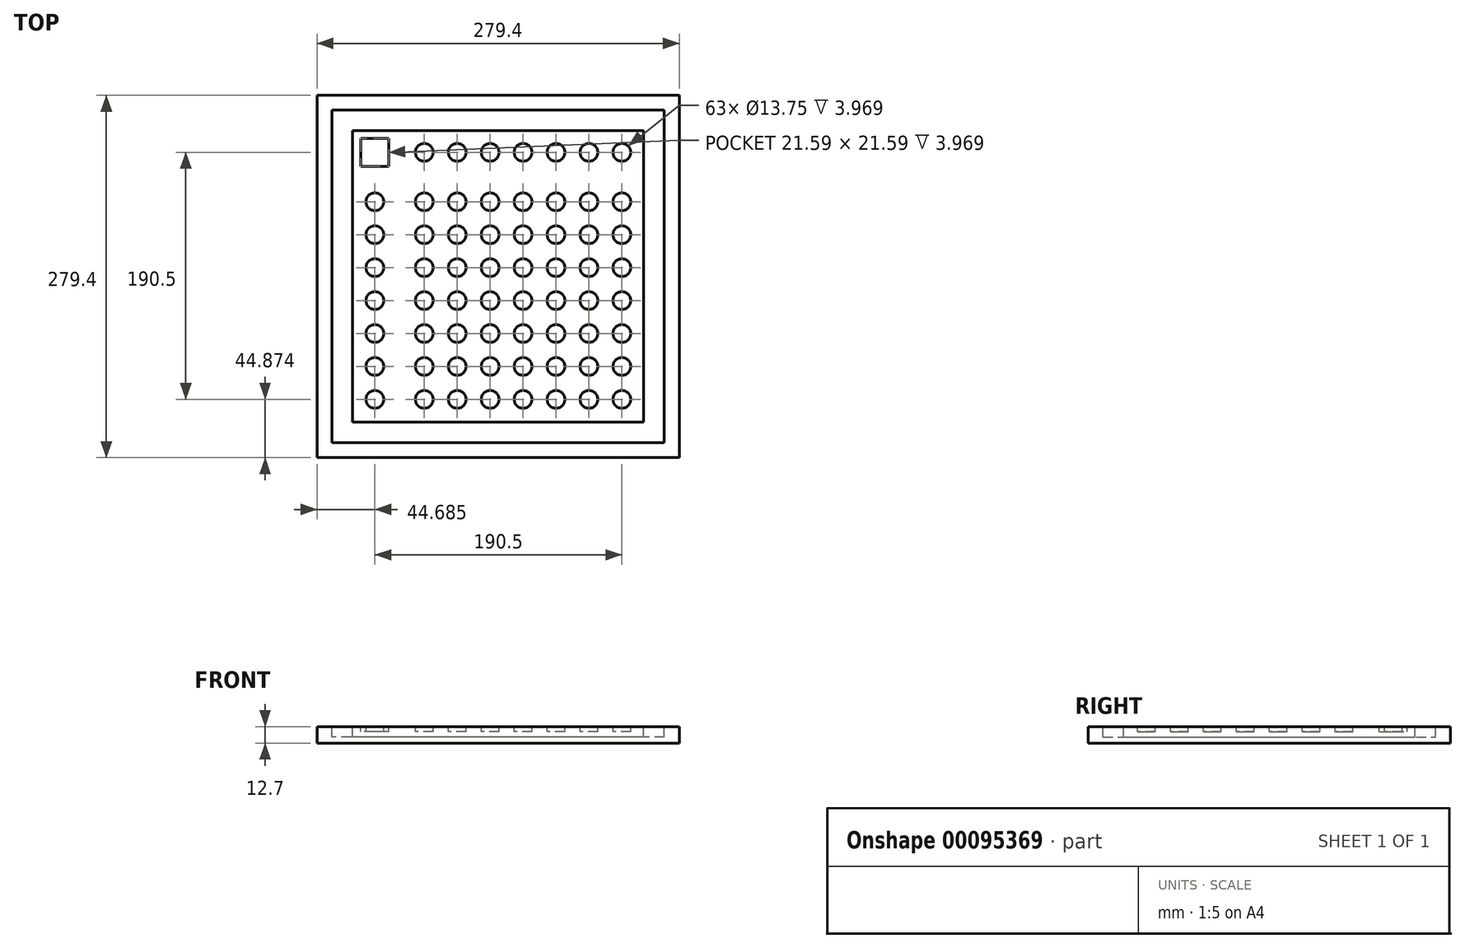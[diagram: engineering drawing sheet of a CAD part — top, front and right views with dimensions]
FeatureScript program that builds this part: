
annotation { "Feature Type Name" : "Feature", "Feature Type Description" : "" }
export const myFeature = defineFeature(function(context is Context, id is Id, definition is map)
    precondition{}
    {
        {
            var Q0;
            Q0=qCreatedBy(makeId("Top.planeOp"),FACE);
            var sketch = newSketch(context, id + "F0", { "sketchPlane" : qUnion([Q0])});
            skLineSegment(sketch, "E0.bottom", {"start": v(-139.7, -139.7) * mm, "end": v(139.7, -139.7) * mm});
            skLineSegment(sketch, "E0.top", {"start": v(-139.7, 139.7) * mm, "end": v(139.7, 139.7) * mm});
            skLineSegment(sketch, "E0.left", {"start": v(-139.7, -139.7) * mm, "end": v(-139.7, 139.7) * mm});
            skLineSegment(sketch, "E0.right", {"start": v(139.7, -139.7) * mm, "end": v(139.7, 139.7) * mm});
            skPoint(sketch, "E0.middle", {"position": v(0, 0) * mm});
            skSolve(sketch);
        }
        {
            var Q0;
            Q0 = qSketchRegion(id + "F0", true);
            extrude(context, id + "F1", {"entities" : qUnion([Q0]), "oppositeDirection" : true, "depth" : 12.7 * mm});
        }
        {
            var Q0;
            Q0=qCreatedBy(makeId("Top.planeOp"),FACE);
            var sketch = newSketch(context, id + "F2", { "sketchPlane" : qUnion([Q0])});
            skCircle(sketch, "E1", {"center": v(-56.91, -94.83) * mm, "radius": 6.87 * mm});
            skPoint(sketch, "E1.first.point", {"position": v(-63.74, -95.66) * mm});
            skPoint(sketch, "E1.second.point", {"position": v(-63.74, -95.66) * mm});
            skPoint(sketch, "E1.third.point", {"position": v(-63.74, -95.66) * mm});
            skCircle(sketch, "E2.0.1.0", {"center": v(-56.91, -69.43) * mm, "radius": 6.87 * mm});
            skCircle(sketch, "E2.0.2.0", {"center": v(-56.91, -44.03) * mm, "radius": 6.87 * mm});
            skCircle(sketch, "E2.0.3.0", {"center": v(-56.91, -18.63) * mm, "radius": 6.87 * mm});
            skCircle(sketch, "E2.0.4.0", {"center": v(-56.91, 6.77) * mm, "radius": 6.87 * mm});
            skCircle(sketch, "E2.0.5.0", {"center": v(-56.91, 32.17) * mm, "radius": 6.87 * mm});
            skCircle(sketch, "E2.0.6.0", {"center": v(-56.91, 57.57) * mm, "radius": 6.87 * mm});
            skCircle(sketch, "E2.1.0.0", {"center": v(-31.51, -94.83) * mm, "radius": 6.87 * mm});
            skCircle(sketch, "E2.1.1.0", {"center": v(-31.51, -69.43) * mm, "radius": 6.87 * mm});
            skCircle(sketch, "E2.1.2.0", {"center": v(-31.51, -44.03) * mm, "radius": 6.87 * mm});
            skCircle(sketch, "E2.1.3.0", {"center": v(-31.51, -18.63) * mm, "radius": 6.87 * mm});
            skCircle(sketch, "E2.1.4.0", {"center": v(-31.51, 6.77) * mm, "radius": 6.87 * mm});
            skCircle(sketch, "E2.1.5.0", {"center": v(-31.51, 32.17) * mm, "radius": 6.87 * mm});
            skCircle(sketch, "E2.1.6.0", {"center": v(-31.51, 57.57) * mm, "radius": 6.87 * mm});
            skCircle(sketch, "E2.2.0.0", {"center": v(-6.11, -94.83) * mm, "radius": 6.87 * mm});
            skCircle(sketch, "E2.2.1.0", {"center": v(-6.11, -69.43) * mm, "radius": 6.87 * mm});
            skCircle(sketch, "E2.2.2.0", {"center": v(-6.11, -44.03) * mm, "radius": 6.87 * mm});
            skCircle(sketch, "E2.2.3.0", {"center": v(-6.11, -18.63) * mm, "radius": 6.87 * mm});
            skCircle(sketch, "E2.2.4.0", {"center": v(-6.11, 6.77) * mm, "radius": 6.87 * mm});
            skCircle(sketch, "E2.2.5.0", {"center": v(-6.11, 32.17) * mm, "radius": 6.87 * mm});
            skCircle(sketch, "E2.2.6.0", {"center": v(-6.11, 57.57) * mm, "radius": 6.87 * mm});
            skCircle(sketch, "E2.3.0.0", {"center": v(19.29, -94.83) * mm, "radius": 6.87 * mm});
            skCircle(sketch, "E2.3.1.0", {"center": v(19.29, -69.43) * mm, "radius": 6.87 * mm});
            skCircle(sketch, "E2.3.2.0", {"center": v(19.29, -44.03) * mm, "radius": 6.87 * mm});
            skCircle(sketch, "E2.3.3.0", {"center": v(19.29, -18.63) * mm, "radius": 6.87 * mm});
            skCircle(sketch, "E2.3.4.0", {"center": v(19.29, 6.77) * mm, "radius": 6.87 * mm});
            skCircle(sketch, "E2.3.5.0", {"center": v(19.29, 32.17) * mm, "radius": 6.87 * mm});
            skCircle(sketch, "E2.3.6.0", {"center": v(19.29, 57.57) * mm, "radius": 6.87 * mm});
            skCircle(sketch, "E2.4.0.0", {"center": v(44.69, -94.83) * mm, "radius": 6.87 * mm});
            skCircle(sketch, "E2.4.1.0", {"center": v(44.69, -69.43) * mm, "radius": 6.87 * mm});
            skCircle(sketch, "E2.4.2.0", {"center": v(44.69, -44.03) * mm, "radius": 6.87 * mm});
            skCircle(sketch, "E2.4.3.0", {"center": v(44.69, -18.63) * mm, "radius": 6.87 * mm});
            skCircle(sketch, "E2.4.4.0", {"center": v(44.69, 6.77) * mm, "radius": 6.87 * mm});
            skCircle(sketch, "E2.4.5.0", {"center": v(44.69, 32.17) * mm, "radius": 6.87 * mm});
            skCircle(sketch, "E2.4.6.0", {"center": v(44.69, 57.57) * mm, "radius": 6.87 * mm});
            skCircle(sketch, "E2.5.0.0", {"center": v(70.09, -94.83) * mm, "radius": 6.87 * mm});
            skCircle(sketch, "E2.5.1.0", {"center": v(70.09, -69.43) * mm, "radius": 6.87 * mm});
            skCircle(sketch, "E2.5.2.0", {"center": v(70.09, -44.03) * mm, "radius": 6.87 * mm});
            skCircle(sketch, "E2.5.3.0", {"center": v(70.09, -18.63) * mm, "radius": 6.87 * mm});
            skCircle(sketch, "E2.5.4.0", {"center": v(70.09, 6.77) * mm, "radius": 6.87 * mm});
            skCircle(sketch, "E2.5.5.0", {"center": v(70.09, 32.17) * mm, "radius": 6.87 * mm});
            skCircle(sketch, "E2.5.6.0", {"center": v(70.09, 57.57) * mm, "radius": 6.87 * mm});
            skCircle(sketch, "E2.6.0.0", {"center": v(95.49, -94.83) * mm, "radius": 6.87 * mm});
            skCircle(sketch, "E2.6.1.0", {"center": v(95.49, -69.43) * mm, "radius": 6.87 * mm});
            skCircle(sketch, "E2.6.2.0", {"center": v(95.49, -44.03) * mm, "radius": 6.87 * mm});
            skCircle(sketch, "E2.6.3.0", {"center": v(95.49, -18.63) * mm, "radius": 6.87 * mm});
            skCircle(sketch, "E2.6.4.0", {"center": v(95.49, 6.77) * mm, "radius": 6.87 * mm});
            skCircle(sketch, "E2.6.5.0", {"center": v(95.49, 32.17) * mm, "radius": 6.87 * mm});
            skCircle(sketch, "E2.6.6.0", {"center": v(95.49, 57.57) * mm, "radius": 6.87 * mm});
            skLineSegment(sketch, "E2.direction1", {"start": v(-56.91, -94.83) * mm, "end": v(-31.51, -94.83) * mm, "construction": true});
            skLineSegment(sketch, "E2.direction2", {"start": v(-56.91, -94.83) * mm, "end": v(-56.91, -69.43) * mm, "construction": true});
            skCircle(sketch, "E3", {"center": v(-95.01, -94.83) * mm, "radius": 6.87 * mm});
            skPoint(sketch, "E3.first.point", {"position": v(-101.85, -94.1) * mm});
            skPoint(sketch, "E3.second.point", {"position": v(-101.85, -94.1) * mm});
            skPoint(sketch, "E3.third.point", {"position": v(-101.85, -94.1) * mm});
            skLineSegment(sketch, "E4.direction2", {"start": v(-95.01, -94.83) * mm, "end": v(-95.01, -74.61) * mm, "construction": true});
            skCircle(sketch, "E5", {"center": v(95.49, 95.67) * mm, "radius": 6.87 * mm});
            skPoint(sketch, "E5.first.point", {"position": v(100.9, 99.9) * mm});
            skPoint(sketch, "E5.second.point", {"position": v(100.9, 99.9) * mm});
            skPoint(sketch, "E5.third.point", {"position": v(100.9, 99.9) * mm});
            skCircle(sketch, "E6.1.0.0", {"center": v(70.09, 95.67) * mm, "radius": 6.87 * mm});
            skCircle(sketch, "E6.2.0.0", {"center": v(44.69, 95.67) * mm, "radius": 6.87 * mm});
            skCircle(sketch, "E6.3.0.0", {"center": v(19.29, 95.67) * mm, "radius": 6.87 * mm});
            skCircle(sketch, "E6.4.0.0", {"center": v(-6.11, 95.67) * mm, "radius": 6.87 * mm});
            skCircle(sketch, "E6.5.0.0", {"center": v(-31.51, 95.67) * mm, "radius": 6.87 * mm});
            skCircle(sketch, "E6.6.0.0", {"center": v(-56.91, 95.67) * mm, "radius": 6.87 * mm});
            skLineSegment(sketch, "E6.direction1", {"start": v(95.49, 95.67) * mm, "end": v(70.09, 95.67) * mm, "construction": true});
            skPoint(sketch, "E7.first.point", {"position": v(-88.23, 95.76) * mm});
            skPoint(sketch, "E7.second.point", {"position": v(-88.23, 95.76) * mm});
            skPoint(sketch, "E7.third.point", {"position": v(-88.23, 95.76) * mm});
            skPoint(sketch, "E8.middle", {"position": v(11.35, 8.36) * mm});
            skCircle(sketch, "E9.0.1.0", {"center": v(-95.01, -69.43) * mm, "radius": 6.87 * mm});
            skCircle(sketch, "E9.0.2.0", {"center": v(-95.01, -44.03) * mm, "radius": 6.87 * mm});
            skCircle(sketch, "E9.0.3.0", {"center": v(-95.01, -18.63) * mm, "radius": 6.87 * mm});
            skCircle(sketch, "E9.0.4.0", {"center": v(-95.01, 6.77) * mm, "radius": 6.87 * mm});
            skCircle(sketch, "E9.0.5.0", {"center": v(-95.01, 32.17) * mm, "radius": 6.87 * mm});
            skCircle(sketch, "E9.0.6.0", {"center": v(-95.01, 57.57) * mm, "radius": 6.87 * mm});
            skLineSegment(sketch, "E9.direction1", {"start": v(-95.01, -94.83) * mm, "end": v(-77.79, -94.83) * mm, "construction": true});
            skLineSegment(sketch, "E9.direction2", {"start": v(-95.01, -94.83) * mm, "end": v(-95.01, -69.43) * mm, "construction": true});
            skPoint(sketch, "E10.endSnap0", {"position": v(108.7, 95.74) * mm});
            skLineSegment(sketch, "E11.bottom", {"start": v(-84.22, 84.88) * mm, "end": v(-105.8, 84.88) * mm});
            skLineSegment(sketch, "E11.top", {"start": v(-84.22, 106.47) * mm, "end": v(-105.8, 106.47) * mm});
            skLineSegment(sketch, "E11.left", {"start": v(-84.22, 84.88) * mm, "end": v(-84.22, 106.47) * mm});
            skLineSegment(sketch, "E11.right", {"start": v(-105.8, 84.88) * mm, "end": v(-105.8, 106.47) * mm});
            skPoint(sketch, "E11.middle", {"position": v(-95.01, 95.67) * mm});
            skSolve(sketch);
        }
        {
            var Q0;
            Q0 = qSketchRegion(id + "F2", true);
            extrude(context, id + "F3", {"entities" : qUnion([Q0]), "operationType" : NewBodyOperationType.REMOVE, "oppositeDirection" : true, "depth" : 3.97 * mm});
        }
        {
            var Q0;
            Q0=qCreatedBy(makeId("Top.planeOp"),FACE);
            var sketch = newSketch(context, id + "F4", { "sketchPlane" : qUnion([Q0])});
            skLineSegment(sketch, "E12.bottom", {"start": v(112.28, -112.28) * mm, "end": v(-112.28, -112.28) * mm});
            skLineSegment(sketch, "E12.top", {"start": v(112.28, 112.28) * mm, "end": v(-112.28, 112.28) * mm});
            skLineSegment(sketch, "E12.left", {"start": v(112.28, -112.28) * mm, "end": v(112.28, 112.28) * mm});
            skLineSegment(sketch, "E12.right", {"start": v(-112.28, -112.28) * mm, "end": v(-112.28, 112.28) * mm});
            skPoint(sketch, "E12.middle", {"position": v(0, 0) * mm});
            skLineSegment(sketch, "E13.bottom", {"start": v(128.16, -128.16) * mm, "end": v(-128.16, -128.16) * mm});
            skLineSegment(sketch, "E13.top", {"start": v(128.16, 128.16) * mm, "end": v(-128.16, 128.16) * mm});
            skLineSegment(sketch, "E13.left", {"start": v(128.16, -128.16) * mm, "end": v(128.16, 128.16) * mm});
            skLineSegment(sketch, "E13.right", {"start": v(-128.16, -128.16) * mm, "end": v(-128.16, 128.16) * mm});
            skSolve(sketch);
        }
        {
            var Q0;
            Q0 = qSketchRegion(id + "F4", true);
            extrude(context, id + "F5", {"entities" : qUnion([Q0]), "operationType" : NewBodyOperationType.REMOVE, "oppositeDirection" : true, "depth" : 7.94 * mm});
        }
    });
